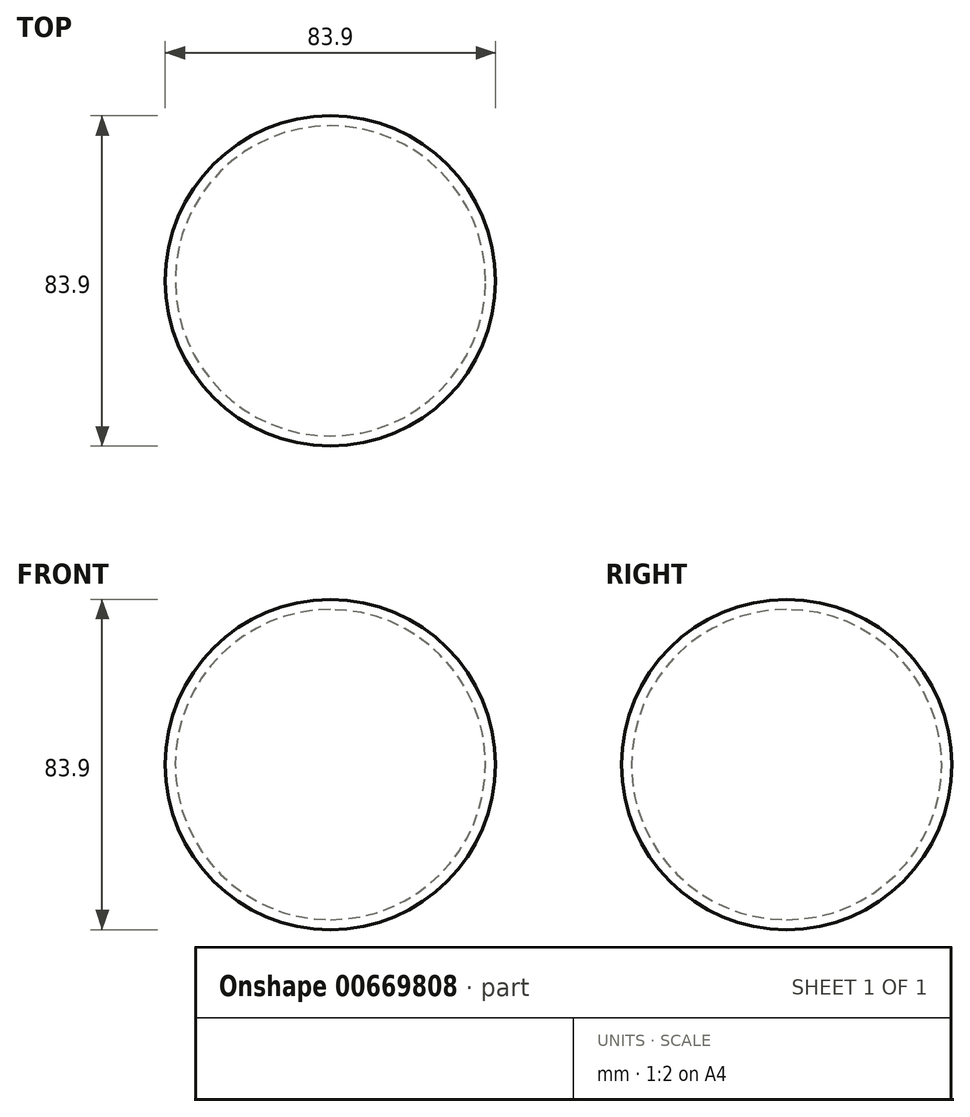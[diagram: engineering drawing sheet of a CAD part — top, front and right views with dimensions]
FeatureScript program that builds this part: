
annotation { "Feature Type Name" : "Feature", "Feature Type Description" : "" }
export const myFeature = defineFeature(function(context is Context, id is Id, definition is map)
    precondition{}
    {
        {
            var Q0;
            Q0=qCreatedBy(makeId("Front.planeOp"),FACE);
            var sketch = newSketch(context, id + "F0", { "sketchPlane" : qUnion([Q0])});
            skArc(sketch, "E0", {"start": v(0, -41.95) * mm, "mid": v(41.95, 0) * mm, "end": v(0, 41.95) * mm});
            skLineSegment(sketch, "E1", {"start": v(0, 41.95) * mm, "end": v(0, -41.95) * mm});
            skSolve(sketch);
        }
        {
            var Q0;
            Q0=makeQuery(id+"F0.imprint","IMPRINT",FACE,{"disambiguationData":[TD([[makeQuery(id+"F0.imprint","IMPRINT",EDGE,{"derivedFrom":sQuery(id+"F0.wireOp",EDGE,"E0")}),1.0]])]});
            var Q1;
            Q1=sQuery(id+"F0.wireOp",EDGE,"E1");
            revolve(context, id + "F1", {"entities" : qUnion([Q0]), "axis" : qUnion([Q1]), "revolveType" : RevolveType.FULL});
        }
        {
            var Q0;
            Q0=makeQuery(id+"F1.opRevolve","SWEPT_FACE",FACE,{"disambiguationData":[OSD([sQuery(id+"F0.wireOp",EDGE,"E0")])]});
            var Q1;
            Q1=makeQuery(id+"F1.opRevolve","SWEPT_BODY",BODY,{"disambiguationData":[OSD([sQuery(id+"F0.wireOp",EDGE,"E0"),sQuery(id+"F0.wireOp",EDGE,"E1")])]});
            shell(context, id + "F2", {"isHollow" : true, "entities" : qUnion([Q0]), "parts" : qUnion([Q1]), "thickness" : 2.54 * mm});
        }
    });
